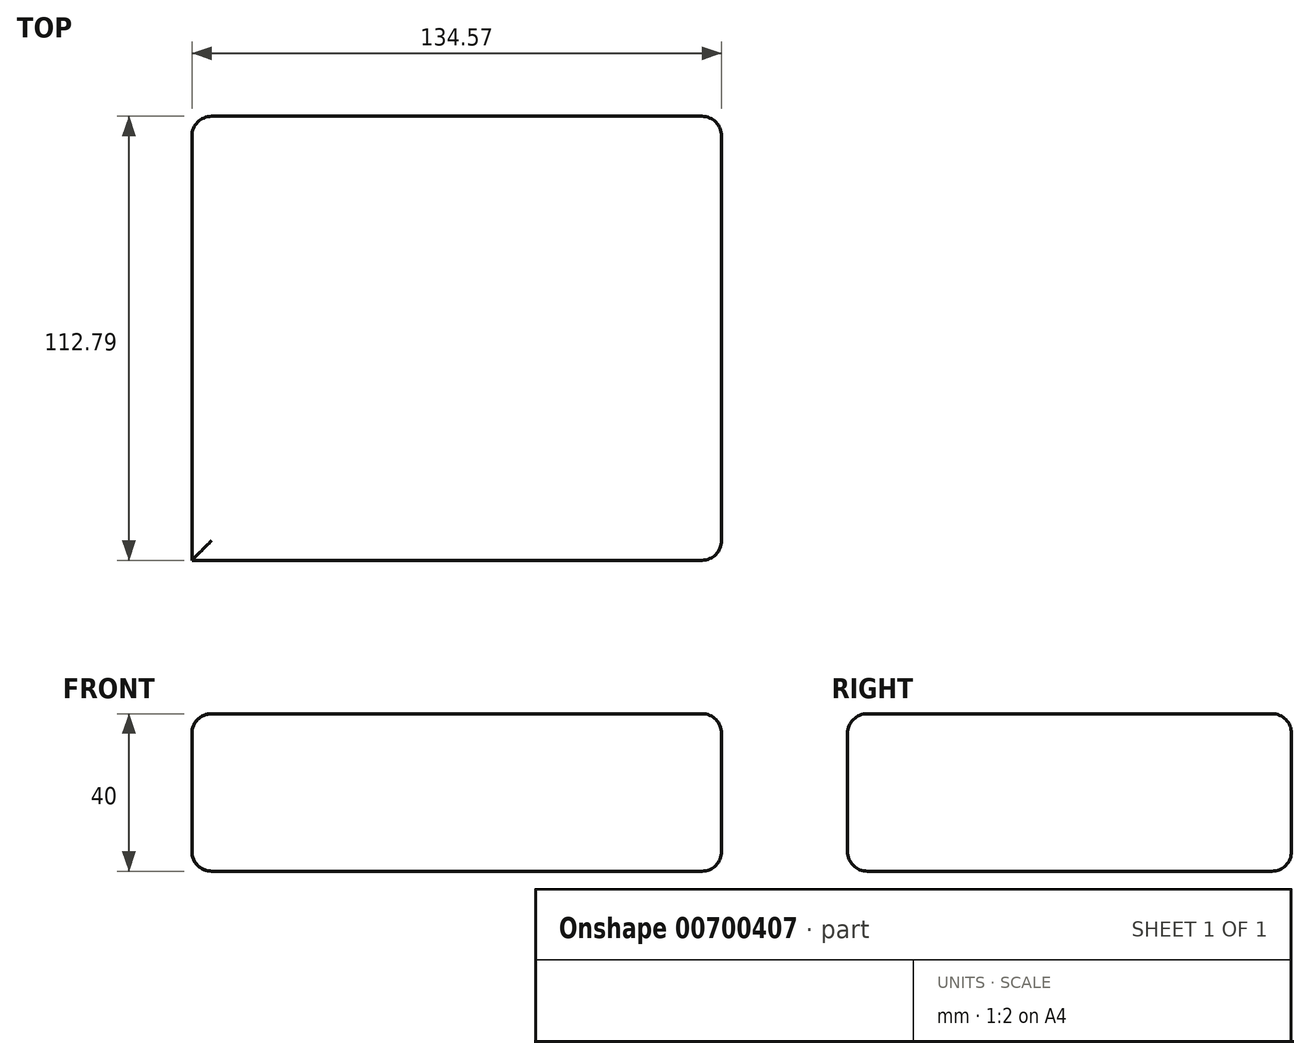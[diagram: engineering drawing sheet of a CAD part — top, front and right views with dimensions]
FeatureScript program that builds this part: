
annotation { "Feature Type Name" : "Feature", "Feature Type Description" : "" }
export const myFeature = defineFeature(function(context is Context, id is Id, definition is map)
    precondition{}
    {
        {
            var Q0;
            Q0=qCreatedBy(makeId("Top.planeOp"),FACE);
            var sketch = newSketch(context, id + "F0", { "sketchPlane" : qUnion([Q0])});
            skLineSegment(sketch, "E0.bottom", {"start": v(134.57, 0) * mm, "end": v(0, 0) * mm});
            skLineSegment(sketch, "E0.top", {"start": v(134.57, -87.39) * mm, "end": v(0, -87.39) * mm});
            skLineSegment(sketch, "E0.left", {"start": v(134.57, 0) * mm, "end": v(134.57, -87.39) * mm});
            skLineSegment(sketch, "E0.right", {"start": v(0, 0) * mm, "end": v(0, -87.39) * mm});
            skSolve(sketch);
        }
        {
            var Q0;
            Q0=makeQuery(id+"F0.imprint","IMPRINT",FACE,{"disambiguationData":[TD([[makeQuery(id+"F0.imprint","IMPRINT",EDGE,{"derivedFrom":sQuery(id+"F0.wireOp",EDGE,"E0.bottom")}),1.0]])]});
            extrude(context, id + "F1", {"entities" : qUnion([Q0]), "depth" : 40 * mm, "offsetDistance" : 25.4 * mm});
        }
        {
            var Q0;
            Q0=makeQuery(id+"F1.opExtrude","SWEPT_FACE",FACE,{"disambiguationData":[OSD([sQuery(id+"F0.wireOp",EDGE,"E0.top")])]});
            extrude(context, id + "F2", {"entities" : qUnion([Q0]), "operationType" : NewBodyOperationType.ADD, "depth" : 25.4 * mm, "offsetDistance" : 25.4 * mm});
        }
        {
            var Q0;
            {var subQ0=sQuery(id+"F0.wireOp",EDGE,"E0.top");Q0=makeQuery(id+"F2.boolean.opBoolean","MERGE",FACE,{"derivedFrom":[makeQuery(id+"F1.opExtrude","CAP_FACE",FACE,{"disambiguationData":[OSD([sQuery(id+"F0.wireOp",EDGE,"E0.bottom"),subQ0,sQuery(id+"F0.wireOp",EDGE,"E0.left"),sQuery(id+"F0.wireOp",EDGE,"E0.right")])],"isStart":false}),makeQuery(id+"F2.opExtrude","SWEPT_FACE",FACE,{"disambiguationData":[OSD([subQ0]),TDD([makeQuery(id+"F1.opExtrude","CAP_EDGE",EDGE,{"disambiguationData":[OSD([subQ0])],"isStart":false})])]})]});}
            var Q1;
            {var subQ0=sQuery(id+"F0.wireOp",EDGE,"E0.top");Q1=makeQuery(id+"F2.boolean.opBoolean","MERGE",FACE,{"derivedFrom":[makeQuery(id+"F1.opExtrude","CAP_FACE",FACE,{"disambiguationData":[OSD([sQuery(id+"F0.wireOp",EDGE,"E0.bottom"),subQ0,sQuery(id+"F0.wireOp",EDGE,"E0.left"),sQuery(id+"F0.wireOp",EDGE,"E0.right")])],"isStart":true}),makeQuery(id+"F2.opExtrude","SWEPT_FACE",FACE,{"disambiguationData":[OSD([subQ0]),TDD([makeQuery(id+"F1.opExtrude","CAP_EDGE",EDGE,{"disambiguationData":[OSD([subQ0])],"isStart":true})])]})]});}
            var Q2;
            {var subQ0=sQuery(id+"F0.wireOp",EDGE,"E0.left");Q2=makeQuery(id+"F2.boolean.opBoolean","MERGE",FACE,{"derivedFrom":[makeQuery(id+"F1.opExtrude","SWEPT_FACE",FACE,{"disambiguationData":[OSD([subQ0])]}),makeQuery(id+"F2.opExtrude","SWEPT_FACE",FACE,{"disambiguationData":[OSD([sQuery(id+"F0.wireOp",EDGE,"E0.top"),subQ0])]})]});}
            var Q3;
            Q3=makeQuery(id+"F1.opExtrude","SWEPT_FACE",FACE,{"disambiguationData":[OSD([sQuery(id+"F0.wireOp",EDGE,"E0.bottom")])]});
            var Q4;
            Q4=makeQuery(id+"FEjrc8gam4EeMBc_1.opSweep","SWEPT_FACE",FACE,{"disambiguationData":[OSD([sQuery(id+"F0.wireOp",EDGE,"E0.top"),sQuery(id+"F0.wireOp",EDGE,"E0.right")])]});
            fillet(context, id + "F3", {"entities" : qUnion([Q0, Q1, Q2, Q3, Q4]), "radius" : 5 * mm, "tangentPropagation" : true, "allowEdgeOverflow" : false});
        }
    });
